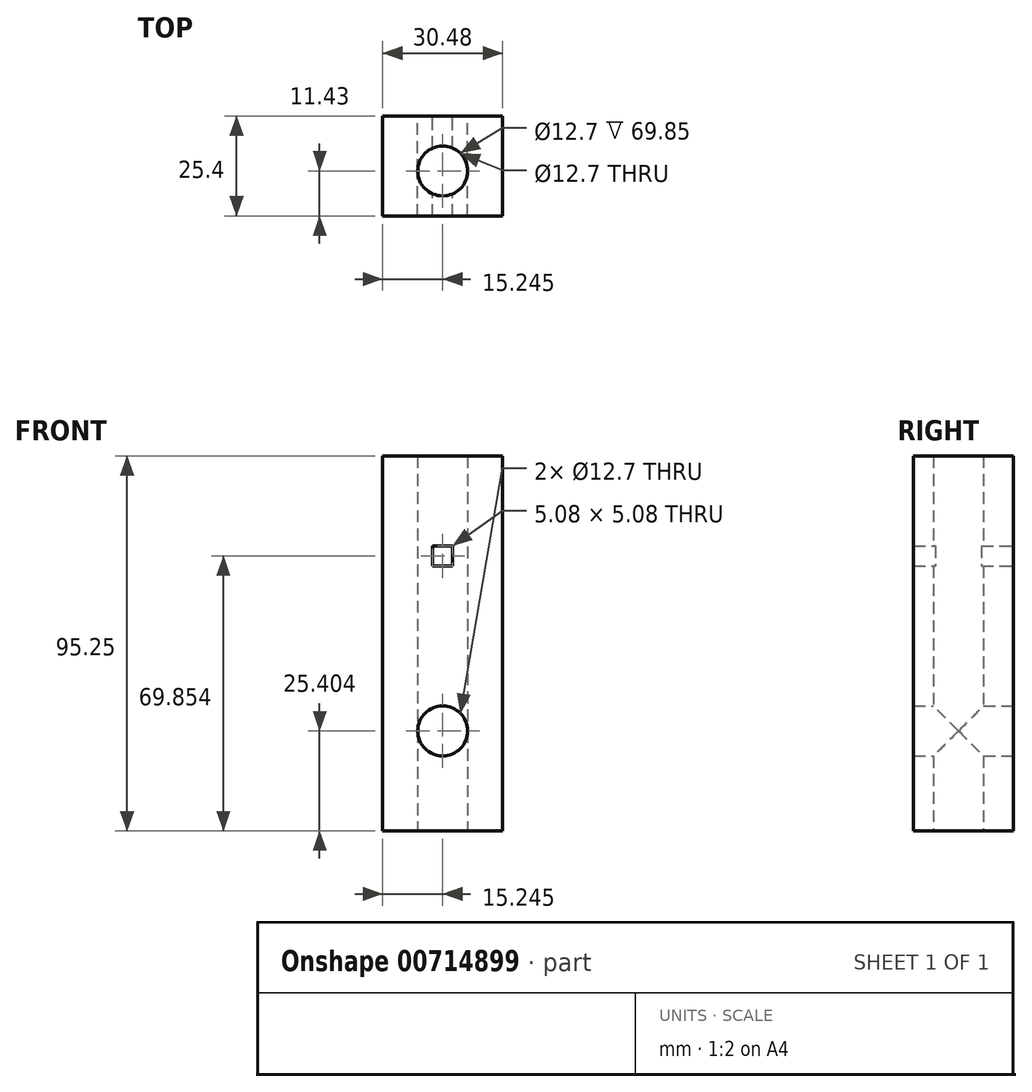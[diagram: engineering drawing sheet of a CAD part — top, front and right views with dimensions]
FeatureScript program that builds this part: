
annotation { "Feature Type Name" : "Feature", "Feature Type Description" : "" }
export const myFeature = defineFeature(function(context is Context, id is Id, definition is map)
    precondition{}
    {
        {
            var Q0;
            Q0=qCreatedBy(makeId("Front.planeOp"),FACE);
            var sketch = newSketch(context, id + "F0", { "sketchPlane" : qUnion([Q0])});
            skLineSegment(sketch, "E0.bottom", {"start": v(-290.95, 52.58) * mm, "end": v(-260.47, 52.58) * mm});
            skLineSegment(sketch, "E0.top", {"start": v(-290.95, -42.67) * mm, "end": v(-260.47, -42.67) * mm});
            skLineSegment(sketch, "E0.left", {"start": v(-290.95, 52.58) * mm, "end": v(-290.95, -42.67) * mm});
            skLineSegment(sketch, "E0.right", {"start": v(-260.47, 52.58) * mm, "end": v(-260.47, -42.67) * mm});
            skLineSegment(sketch, "E1", {"start": v(-275.7, 52.58) * mm, "end": v(-275.7, -42.67) * mm, "construction": true});
            skLineSegment(sketch, "E2.bottom", {"start": v(-273.17, 24.64) * mm, "end": v(-278.25, 24.64) * mm});
            skLineSegment(sketch, "E2.top", {"start": v(-273.17, 29.72) * mm, "end": v(-278.25, 29.72) * mm});
            skLineSegment(sketch, "E2.left", {"start": v(-273.17, 24.64) * mm, "end": v(-273.17, 29.72) * mm});
            skLineSegment(sketch, "E2.right", {"start": v(-278.25, 24.64) * mm, "end": v(-278.25, 29.72) * mm});
            skPoint(sketch, "E2.middle", {"position": v(-275.7, 27.18) * mm});
            skCircle(sketch, "E3", {"center": v(-275.7, -17.27) * mm, "radius": 6.35 * mm});
            skSolve(sketch);
        }
        {
            var Q0;
            Q0 = qSketchRegion(id + "F0", true);
            extrude(context, id + "F1", {"entities" : qUnion([Q0]), "depth" : 25.4 * mm, "offsetDistance" : 25.4 * mm});
        }
        {
            var Q0;
            Q0=makeQuery(id+"F1.opExtrude","SWEPT_FACE",FACE,{"disambiguationData":[OSD([sQuery(id+"F0.wireOp",EDGE,"E0.top")])]});
            var sketch = newSketch(context, id + "F2", { "sketchPlane" : qUnion([Q0])});
            skLineSegment(sketch, "E4", {"start": v(-275.7, 25.4) * mm, "end": v(-275.7, 0) * mm, "construction": true});
            skCircle(sketch, "E5", {"center": v(-275.7, 13.97) * mm, "radius": 6.35 * mm});
            skSolve(sketch);
        }
        {
            var Q0;
            Q0 = qSketchRegion(id + "F2", true);
            extrude(context, id + "F3", {"entities" : qUnion([Q0]), "operationType" : NewBodyOperationType.REMOVE, "endBound" : BoundingType.THROUGH_ALL, "oppositeDirection" : true, "depth" : 25.4 * mm, "offsetDistance" : 25.4 * mm});
        }
    });
